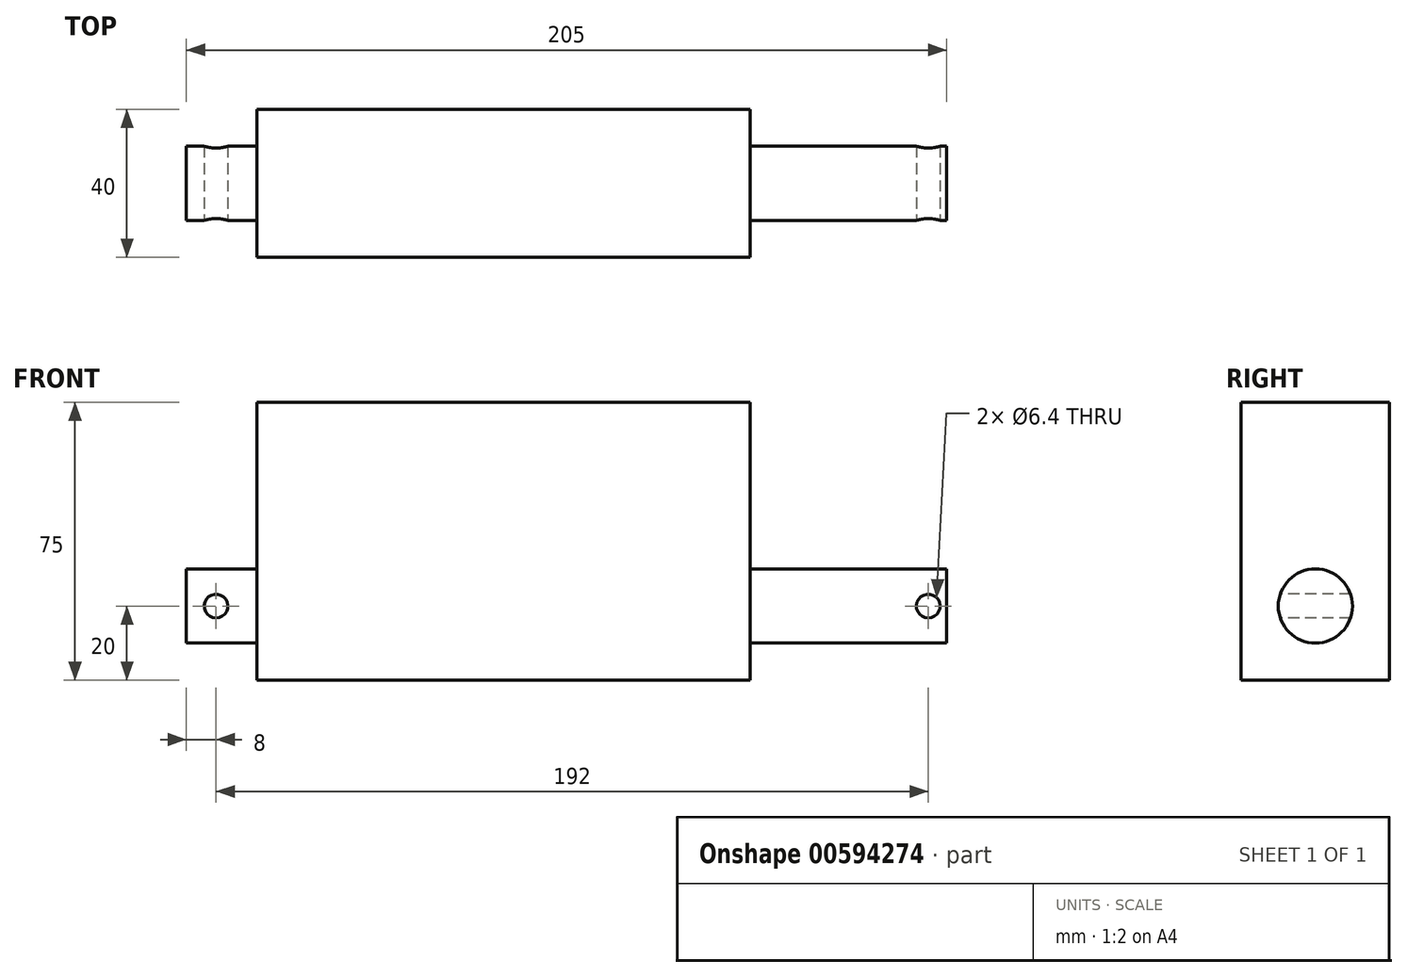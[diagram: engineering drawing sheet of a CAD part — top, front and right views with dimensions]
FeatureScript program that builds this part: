
annotation { "Feature Type Name" : "Feature", "Feature Type Description" : "" }
export const myFeature = defineFeature(function(context is Context, id is Id, definition is map)
    precondition{}
    {
        {
            var Q0;
            Q0=qCreatedBy(makeId("Right.planeOp"),FACE);
            var sketch = newSketch(context, id + "F0", { "sketchPlane" : qUnion([Q0])});
            skLineSegment(sketch, "E0.bottom", {"start": v(20, 37.5) * mm, "end": v(-20, 37.5) * mm});
            skLineSegment(sketch, "E0.top", {"start": v(20, -37.5) * mm, "end": v(-20, -37.5) * mm});
            skLineSegment(sketch, "E0.left", {"start": v(20, 37.5) * mm, "end": v(20, -37.5) * mm});
            skLineSegment(sketch, "E0.right", {"start": v(-20, 37.5) * mm, "end": v(-20, -37.5) * mm});
            skPoint(sketch, "E0.middle", {"position": v(0, 0) * mm});
            skSolve(sketch);
        }
        {
            var Q0;
            Q0 = qSketchRegion(id + "F0", true);
            extrude(context, id + "F1", {"entities" : qUnion([Q0]), "depth" : 133 * mm, "offsetDistance" : 25 * mm});
        }
        {
            var Q0;
            Q0=makeQuery(id+"F1.opExtrude","CAP_FACE",FACE,{"disambiguationData":[OSD([sQuery(id+"F0.wireOp",EDGE,"E0.bottom"),sQuery(id+"F0.wireOp",EDGE,"E0.top"),sQuery(id+"F0.wireOp",EDGE,"E0.left"),sQuery(id+"F0.wireOp",EDGE,"E0.right")])],"isStart":true});
            var sketch = newSketch(context, id + "F2", { "sketchPlane" : qUnion([Q0])});
            skCircle(sketch, "E1", {"center": v(0, -17.5) * mm, "radius": 10 * mm});
            skSolve(sketch);
        }
        {
            var Q0;
            Q0 = qSketchRegion(id + "F2", true);
            extrude(context, id + "F3", {"entities" : qUnion([Q0]), "operationType" : NewBodyOperationType.ADD, "depth" : 19 * mm, "offsetDistance" : 25 * mm});
        }
        {
            var Q0;
            Q0=makeQuery(id+"F1.opExtrude","CAP_FACE",FACE,{"disambiguationData":[OSD([sQuery(id+"F0.wireOp",EDGE,"E0.bottom"),sQuery(id+"F0.wireOp",EDGE,"E0.top"),sQuery(id+"F0.wireOp",EDGE,"E0.left"),sQuery(id+"F0.wireOp",EDGE,"E0.right")])],"isStart":false});
            var sketch = newSketch(context, id + "F4", { "sketchPlane" : qUnion([Q0])});
            skCircle(sketch, "E2", {"center": v(0, -17.5) * mm, "radius": 10 * mm});
            skPoint(sketch, "E2.centerSnap0", {"position": v(0, -37.5) * mm});
            skSolve(sketch);
        }
        {
            var Q0;
            Q0=qCreatedBy(makeId("Front.planeOp"),FACE);
            var sketch = newSketch(context, id + "F5", { "sketchPlane" : qUnion([Q0])});
            skCircle(sketch, "E3", {"center": v(-11, -17.5) * mm, "radius": 3.2 * mm});
            skCircle(sketch, "E4", {"center": v(181, -17.5) * mm, "radius": 3.2 * mm});
            skSolve(sketch);
        }
        {
            var Q0;
            Q0=makeQuery(id+"F4.imprint","IMPRINT",FACE,{"disambiguationData":[TD([[makeQuery(id+"F4.imprint","IMPRINT",EDGE,{"derivedFrom":sQuery(id+"F4.wireOp",EDGE,"E2")}),1.0]])]});
            extrude(context, id + "F6", {"entities" : qUnion([Q0]), "operationType" : NewBodyOperationType.ADD, "depth" : 53 * mm, "offsetDistance" : 25 * mm});
        }
        {
            var Q0;
            Q0 = qSketchRegion(id + "F5", true);
            extrude(context, id + "F7", {"entities" : qUnion([Q0]), "operationType" : NewBodyOperationType.REMOVE, "endBound" : BoundingType.SYMMETRIC, "oppositeDirection" : true, "depth" : 25 * mm, "offsetDistance" : 25 * mm});
        }
    });
